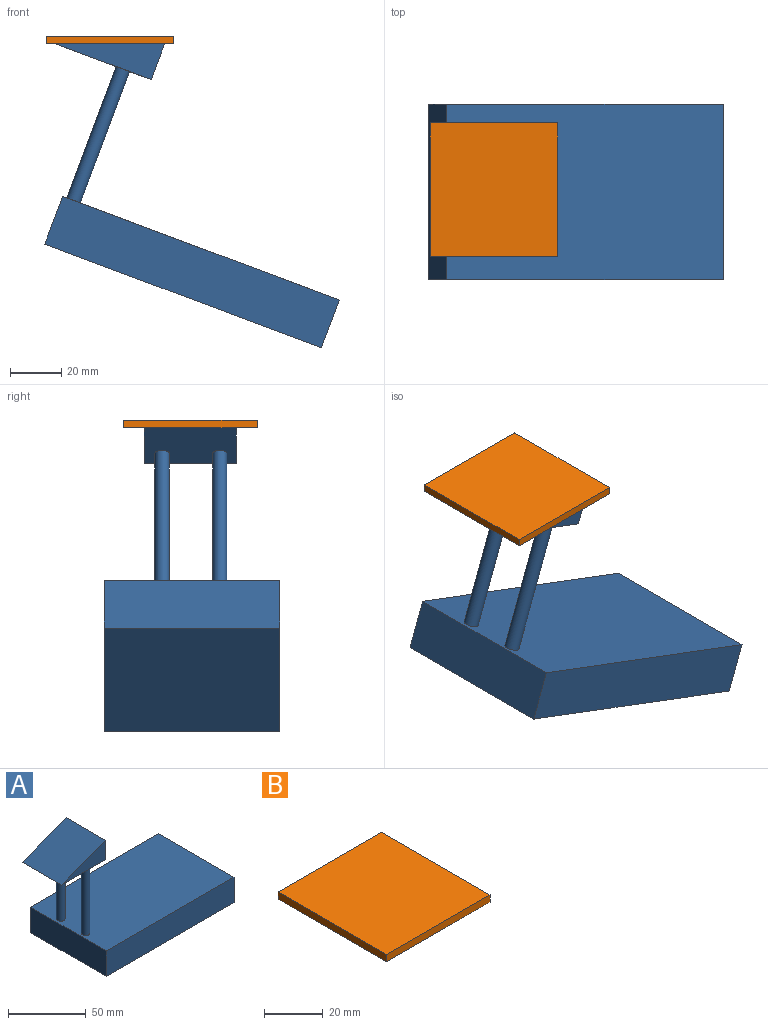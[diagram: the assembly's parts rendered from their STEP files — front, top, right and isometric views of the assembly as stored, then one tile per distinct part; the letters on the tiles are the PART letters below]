
ASSEMBLY  parts=2 mates=1
PART A: 13 faces, bbox 139.3x68.6x90 mm
  f0: plane 68.6x20mm, normal (1,0,0), area 1372mm2, adj f1,f3,f4,f5
  f1: plane 115.77x20mm, normal (0,1,0), area 2315.3mm2, adj f0,f2,f4,f5
  f2: plane 68.6x20mm, normal (-1,0,0), area 1372mm2, adj f1,f3,f4,f5
  f3: plane 115.77x20mm, normal (0,-1,0), area 2315.3mm2, adj f0,f2,f4,f5
  f4: plane 115.77x68.6mm, normal (0,0,1), area 7891.7mm2, adj f0,f1,f2,f3,f6,f7
  f5: plane 115.77x68.6mm, normal (0,0,-1), area 7941.5mm2, adj f0,f1,f2,f3
  f6: cylinder r=2.82mm len=55mm, axis (0,0,-1), area 972.9mm2, adj f4,f11
  f7: cylinder r=2.82mm len=55mm, axis (0,0,-1), area 972.9mm2, adj f4,f11
  f8: plane 35.98x15mm, normal (1,0,0), area 539.7mm2, adj f9,f10,f11,f12
  f9: plane 40x15mm, normal (0,1,0), area 300mm2, adj f8,f11,f12
  f10: plane 40x15mm, normal (0,-1,0), area 300mm2, adj f8,f11,f12
  f11: plane 40x35.98mm, normal (0,0,-1), area 1389.5mm2, adj f6,f7,f8,f9,f10,f12
  f12: plane 40x35.98mm, normal (-0.35,0,0.94), area 1537.2mm2, adj f8,f9,f10,f11
PART B: 6 faces, bbox 50x52.5x3 mm
  f0: plane 52.49x3mm, normal (-1,0,0), area 157.5mm2, adj f1,f3,f4,f5
  f1: plane 50x3mm, normal (0,-1,0), area 150mm2, adj f0,f2,f4,f5
  f2: plane 52.49x3mm, normal (1,0,0), area 157.5mm2, adj f1,f3,f4,f5
  f3: plane 50x3mm, normal (0,1,0), area 150mm2, adj f0,f2,f4,f5
  f4: plane 52.49x50mm, normal (0,0,1), area 2624.7mm2, adj f0,f1,f2,f3
  f5: plane 52.49x50mm, normal (0,0,-1), area 2624.7mm2, adj f0,f1,f2,f3
PLACE A rot(axis=(0,1,0),20.6deg) t=(53.56,25.57,-98.82)mm
PLACE B at identity
MATE fastened A.f12 <-> B.f5  axis (0,0,1) through (25,26.25,0)mm
